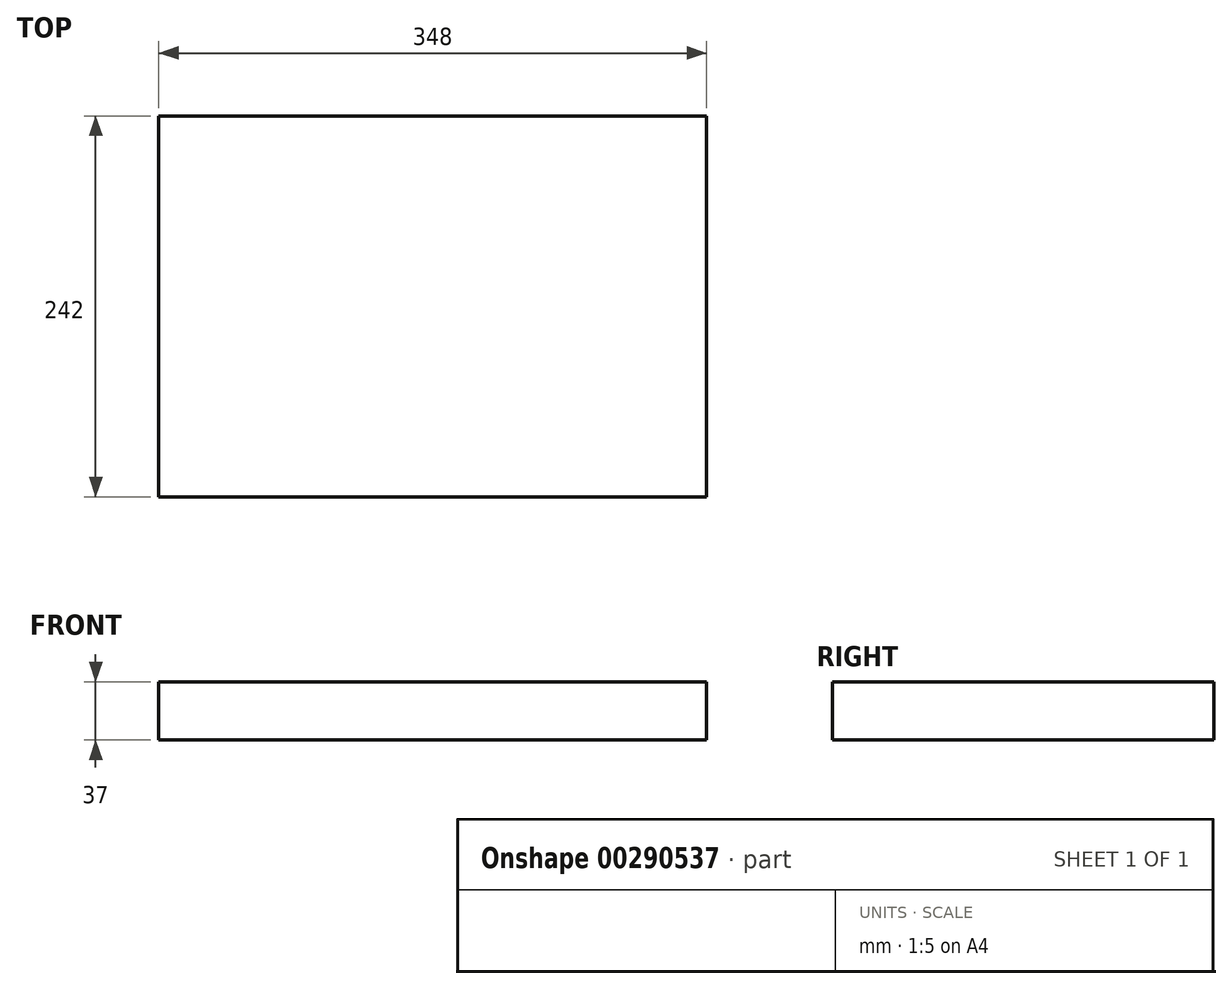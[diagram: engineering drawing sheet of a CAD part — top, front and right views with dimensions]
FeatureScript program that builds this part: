
annotation { "Feature Type Name" : "Feature", "Feature Type Description" : "" }
export const myFeature = defineFeature(function(context is Context, id is Id, definition is map)
    precondition{}
    {
        {
            var Q0;
            Q0=qCreatedBy(makeId("Top.planeOp"),FACE);
            var sketch = newSketch(context, id + "F0", { "sketchPlane" : qUnion([Q0])});
            skLineSegment(sketch, "E0.bottom", {"start": v(174, -121) * mm, "end": v(-174, -121) * mm});
            skLineSegment(sketch, "E0.top", {"start": v(174, 121) * mm, "end": v(-174, 121) * mm});
            skLineSegment(sketch, "E0.left", {"start": v(174, -121) * mm, "end": v(174, 121) * mm});
            skLineSegment(sketch, "E0.right", {"start": v(-174, -121) * mm, "end": v(-174, 121) * mm});
            skPoint(sketch, "E0.middle", {"position": v(0, 0) * mm});
            skSolve(sketch);
        }
        {
            var Q0;
            Q0 = qSketchRegion(id + "F0", true);
            extrude(context, id + "F1", {"entities" : qUnion([Q0]), "depth" : (11.1 + 25.9) * mm});
        }
    });
